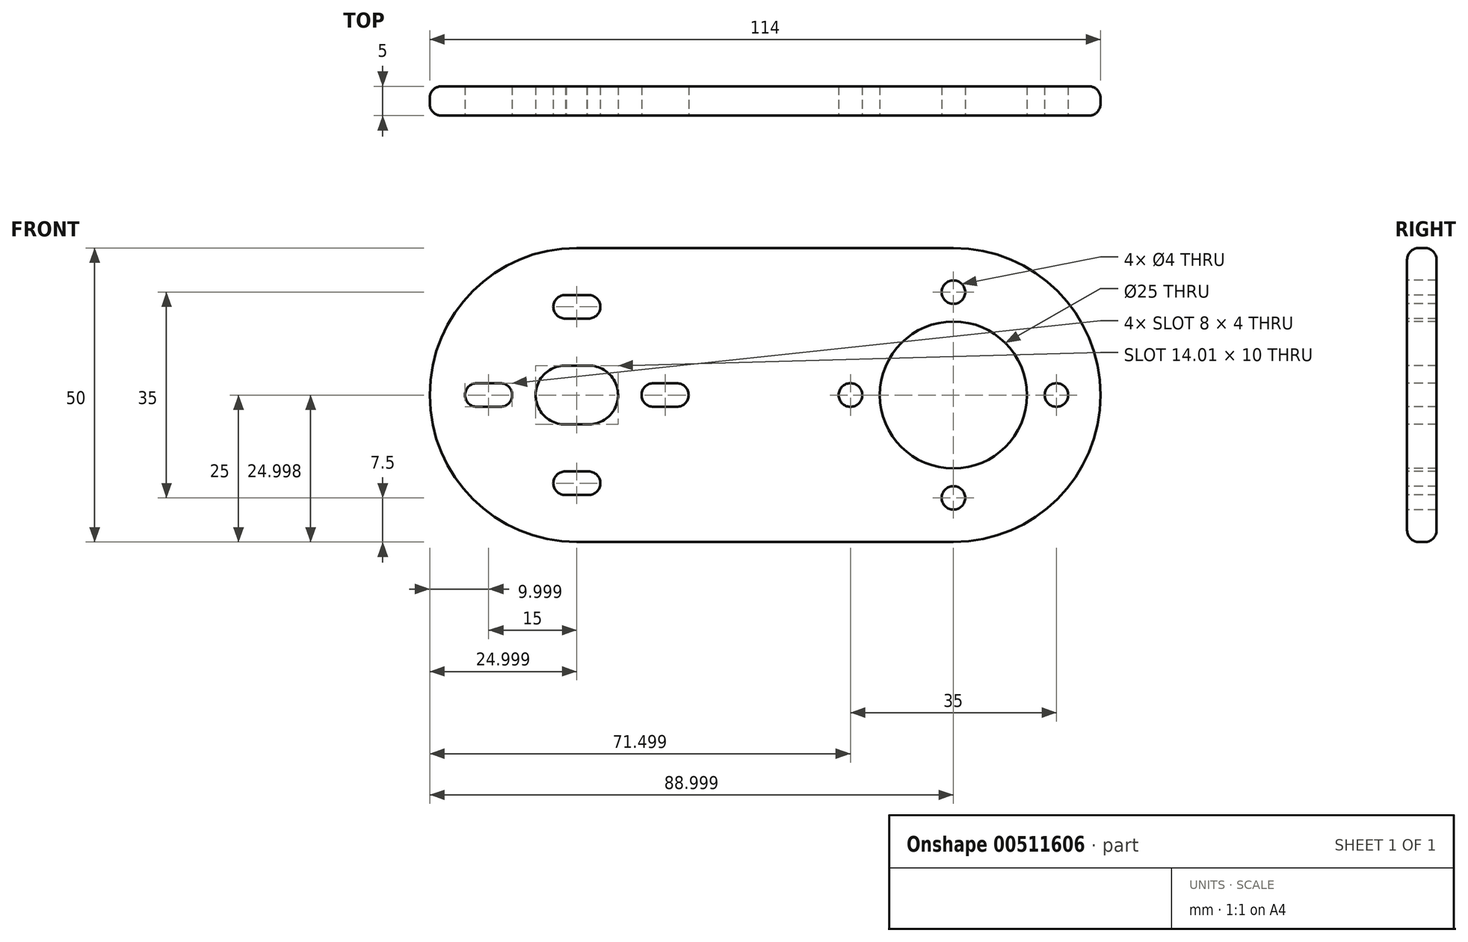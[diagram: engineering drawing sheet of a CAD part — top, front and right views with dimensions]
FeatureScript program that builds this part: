
annotation { "Feature Type Name" : "Feature", "Feature Type Description" : "" }
export const myFeature = defineFeature(function(context is Context, id is Id, definition is map)
    precondition{}
    {
        {
            var Q0;
            Q0=qCreatedBy(makeId("Front.planeOp"),FACE);
            var sketch = newSketch(context, id + "F0", { "sketchPlane" : qUnion([Q0])});
            skArc(sketch, "E0", {"start": v(-33.53, 5) * mm, "mid": v(-33.63, 5) * mm, "end": v(-33.72, 5) * mm});
            skCircle(sketch, "E1", {"center": v(30.47, 0) * mm, "radius": 12.5 * mm});
            skArc(sketch, "E2", {"start": v(-33.53, 25) * mm, "mid": v(-58.53, 0) * mm, "end": v(-33.53, -25) * mm});
            skArc(sketch, "E3", {"start": v(30.47, -25) * mm, "mid": v(55.47, 0) * mm, "end": v(30.47, 25) * mm});
            skLineSegment(sketch, "E4", {"start": v(-33.53, 0) * mm, "end": v(-33.53, 25) * mm, "construction": true});
            skLineSegment(sketch, "E5", {"start": v(30.47, 0) * mm, "end": v(30.47, 25) * mm, "construction": true});
            skLineSegment(sketch, "E6", {"start": v(30.47, 0) * mm, "end": v(30.47, -25) * mm, "construction": true});
            skLineSegment(sketch, "E7", {"start": v(-33.53, 0) * mm, "end": v(-33.53, -13) * mm, "construction": true});
            skLineSegment(sketch, "E8", {"start": v(-33.53, 25) * mm, "end": v(30.47, 25) * mm});
            skLineSegment(sketch, "E9", {"start": v(30.47, -25) * mm, "end": v(-33.53, -25) * mm});
            skPoint(sketch, "E10.center.orphan", {"position": v(-33.53, 15) * mm});
            skPoint(sketch, "E11.center.orphan", {"position": v(-18.53, 0) * mm});
            skArc(sketch, "E12", {"start": v(-18.66, 2) * mm, "mid": v(-33.53, 15) * mm, "end": v(-48.4, 2) * mm, "construction": true});
            skLineSegment(sketch, "E13", {"start": v(-33.53, 0) * mm, "end": v(-35.53, 0) * mm});
            skLineSegment(sketch, "E14", {"start": v(-35.53, 0) * mm, "end": v(-33.53, 0) * mm});
            skLineSegment(sketch, "E15", {"start": v(-31.53, 0) * mm, "end": v(-33.53, 0) * mm});
            skArc(sketch, "E16", {"start": v(-35.34, 5) * mm, "mid": v(-40.53, 0.06) * mm, "end": v(-35.46, -5) * mm});
            skArc(sketch, "E17", {"start": v(-31.8, -5) * mm, "mid": v(-26.53, 0.04) * mm, "end": v(-31.87, 5) * mm});
            skLineSegment(sketch, "E18", {"start": v(-31.17, 5) * mm, "end": v(-35.7, 5) * mm});
            skLineSegment(sketch, "E19", {"start": v(-35.46, -5) * mm, "end": v(-31.8, -5) * mm});
            skArc(sketch, "E20.trimOffspring", {"start": v(-33.53, -5) * mm, "mid": v(-33.53, -5) * mm, "end": v(-33.52, -5) * mm});
            skLineSegment(sketch, "E21", {"start": v(-18.53, 4.2) * mm, "end": v(-18.53, 2) * mm, "construction": true});
            skArc(sketch, "E22", {"start": v(-20.53, 2) * mm, "mid": v(-22.53, 0) * mm, "end": v(-20.53, -2) * mm});
            skArc(sketch, "E23", {"start": v(-16.53, -2) * mm, "mid": v(-14.53, 0) * mm, "end": v(-16.53, 2) * mm});
            skLineSegment(sketch, "E24", {"start": v(-16.53, -2) * mm, "end": v(-20.53, -2) * mm});
            skLineSegment(sketch, "E25", {"start": v(-20.53, 2) * mm, "end": v(-16.53, 2) * mm});
            skLineSegment(sketch, "E26.trimOffspring", {"start": v(-18.53, -2) * mm, "end": v(-18.53, -5.31) * mm, "construction": true});
            skArc(sketch, "E27", {"start": v(-31.53, -17) * mm, "mid": v(-29.53, -15) * mm, "end": v(-31.53, -13) * mm});
            skArc(sketch, "E28", {"start": v(-35.53, -13) * mm, "mid": v(-37.53, -15) * mm, "end": v(-35.53, -17) * mm});
            skLineSegment(sketch, "E29", {"start": v(-35.53, -13) * mm, "end": v(-31.53, -13) * mm});
            skLineSegment(sketch, "E30", {"start": v(-31.53, -17) * mm, "end": v(-35.53, -17) * mm});
            skArc(sketch, "E31.trimOffspring", {"start": v(-29.6, -14.48) * mm, "mid": v(-22.25, -9.89) * mm, "end": v(-18.66, -2) * mm, "construction": true});
            skArc(sketch, "E32", {"start": v(-46.53, -2) * mm, "mid": v(-44.53, 0) * mm, "end": v(-46.53, 2) * mm});
            skArc(sketch, "E33", {"start": v(-50.53, 2) * mm, "mid": v(-52.53, 0) * mm, "end": v(-50.53, -2) * mm});
            skLineSegment(sketch, "E34", {"start": v(-46.53, -2) * mm, "end": v(-50.53, -2) * mm});
            skLineSegment(sketch, "E35", {"start": v(-46.53, 2) * mm, "end": v(-50.53, 2) * mm});
            skArc(sketch, "E36.trimOffspring", {"start": v(-48.4, -2) * mm, "mid": v(-44.81, -9.89) * mm, "end": v(-37.46, -14.48) * mm, "construction": true});
            skPoint(sketch, "E37.center.orphan", {"position": v(-48.53, 0) * mm});
            skArc(sketch, "E38", {"start": v(-31.53, 13) * mm, "mid": v(-29.53, 15) * mm, "end": v(-31.53, 17) * mm});
            skArc(sketch, "E39", {"start": v(-35.53, 17) * mm, "mid": v(-37.53, 15) * mm, "end": v(-35.53, 13) * mm});
            skLineSegment(sketch, "E40", {"start": v(-35.53, 15) * mm, "end": v(-35.53, 13) * mm, "construction": true});
            skLineSegment(sketch, "E41", {"start": v(-35.53, 15) * mm, "end": v(-35.53, 17) * mm, "construction": true});
            skLineSegment(sketch, "E42", {"start": v(-31.53, 15) * mm, "end": v(-31.53, 17) * mm, "construction": true});
            skLineSegment(sketch, "E43", {"start": v(-31.53, 15) * mm, "end": v(-31.53, 13) * mm, "construction": true});
            skLineSegment(sketch, "E44", {"start": v(-35.53, 17) * mm, "end": v(-31.53, 17) * mm});
            skLineSegment(sketch, "E45", {"start": v(-31.53, 13) * mm, "end": v(-35.53, 13) * mm});
            skCircle(sketch, "E46", {"center": v(30.47, 0) * mm, "radius": 17.5 * mm, "construction": true});
            skCircle(sketch, "E47", {"center": v(30.47, 17.5) * mm, "radius": 2 * mm});
            skCircle(sketch, "E48", {"center": v(47.97, 0) * mm, "radius": 2 * mm});
            skCircle(sketch, "E49", {"center": v(30.47, -17.5) * mm, "radius": 2 * mm});
            skCircle(sketch, "E50", {"center": v(12.97, 0) * mm, "radius": 2 * mm});
            skSolve(sketch);
        }
        {
            var Q0;
            Q0 = qSketchRegion(id + "F0", true);
            extrude(context, id + "F1", {"entities" : qUnion([Q0]), "oppositeDirection" : true, "depth" : 5 * mm, "offsetDistance" : 25.4 * mm});
        }
        {
            var Q0;
            Q0=makeQuery(id+"F1.opExtrude","CAP_EDGE",EDGE,{"disambiguationData":[OSD([sQuery(id+"F0.wireOp",EDGE,"E3")])],"isStart":false});
            var Q1;
            {var subQ0=sQuery(id+"F0.wireOp",EDGE,"E3");Q1=makeQuery(id+"FbfvcB8eaHeMghH_1.opFillet","BLEND_EDGE",EDGE,{"blendedFrom":[makeQuery(id+"F1.opExtrude","CAP_EDGE",EDGE,{"disambiguationData":[OSD([subQ0])],"isStart":true}),makeQuery(id+"F1.opExtrude","CAP_FACE",FACE,{"disambiguationData":[OSD([sQuery(id+"F0.wireOp",EDGE,"E1"),sQuery(id+"F0.wireOp",EDGE,"E2"),subQ0,sQuery(id+"F0.wireOp",EDGE,"E8"),sQuery(id+"F0.wireOp",EDGE,"E9"),sQuery(id+"F0.wireOp",EDGE,"E16"),sQuery(id+"F0.wireOp",EDGE,"E17"),sQuery(id+"F0.wireOp",EDGE,"E18"),sQuery(id+"F0.wireOp",EDGE,"E19"),sQuery(id+"F0.wireOp",EDGE,"E20.trimOffspring"),sQuery(id+"F0.wireOp",EDGE,"E22"),sQuery(id+"F0.wireOp",EDGE,"E23"),sQuery(id+"F0.wireOp",EDGE,"E24"),sQuery(id+"F0.wireOp",EDGE,"E25"),sQuery(id+"F0.wireOp",EDGE,"E27"),sQuery(id+"F0.wireOp",EDGE,"E28"),sQuery(id+"F0.wireOp",EDGE,"E29"),sQuery(id+"F0.wireOp",EDGE,"E30"),sQuery(id+"F0.wireOp",EDGE,"E32"),sQuery(id+"F0.wireOp",EDGE,"E33"),sQuery(id+"F0.wireOp",EDGE,"E34"),sQuery(id+"F0.wireOp",EDGE,"E35"),sQuery(id+"F0.wireOp",EDGE,"E38"),sQuery(id+"F0.wireOp",EDGE,"E39"),sQuery(id+"F0.wireOp",EDGE,"E44"),sQuery(id+"F0.wireOp",EDGE,"E45")])],"isStart":true})],"blendedInto":[makeQuery(id+"F1.opExtrude","CAP_FACE",FACE,{"disambiguationData":[OSD([sQuery(id+"F0.wireOp",EDGE,"E1"),sQuery(id+"F0.wireOp",EDGE,"E2"),subQ0,sQuery(id+"F0.wireOp",EDGE,"E8"),sQuery(id+"F0.wireOp",EDGE,"E9"),sQuery(id+"F0.wireOp",EDGE,"E16"),sQuery(id+"F0.wireOp",EDGE,"E17"),sQuery(id+"F0.wireOp",EDGE,"E18"),sQuery(id+"F0.wireOp",EDGE,"E19"),sQuery(id+"F0.wireOp",EDGE,"E20.trimOffspring"),sQuery(id+"F0.wireOp",EDGE,"E22"),sQuery(id+"F0.wireOp",EDGE,"E23"),sQuery(id+"F0.wireOp",EDGE,"E24"),sQuery(id+"F0.wireOp",EDGE,"E25"),sQuery(id+"F0.wireOp",EDGE,"E27"),sQuery(id+"F0.wireOp",EDGE,"E28"),sQuery(id+"F0.wireOp",EDGE,"E29"),sQuery(id+"F0.wireOp",EDGE,"E30"),sQuery(id+"F0.wireOp",EDGE,"E32"),sQuery(id+"F0.wireOp",EDGE,"E33"),sQuery(id+"F0.wireOp",EDGE,"E34"),sQuery(id+"F0.wireOp",EDGE,"E35"),sQuery(id+"F0.wireOp",EDGE,"E38"),sQuery(id+"F0.wireOp",EDGE,"E39"),sQuery(id+"F0.wireOp",EDGE,"E44"),sQuery(id+"F0.wireOp",EDGE,"E45")])],"isStart":true})]});}
            fillet(context, id + "F2", {"entities" : qUnion([Q0, Q1]), "radius" : 2 * mm, "tangentPropagation" : true, "allowEdgeOverflow" : false});
        }
        {
            var Q0;
            Q0=makeQuery(id+"F1.opExtrude","CAP_EDGE",EDGE,{"disambiguationData":[OSD([sQuery(id+"F0.wireOp",EDGE,"E3")])],"isStart":true});
            fillet(context, id + "F3", {"entities" : qUnion([Q0]), "radius" : 2 * mm, "tangentPropagation" : true, "allowEdgeOverflow" : false});
        }
    });
